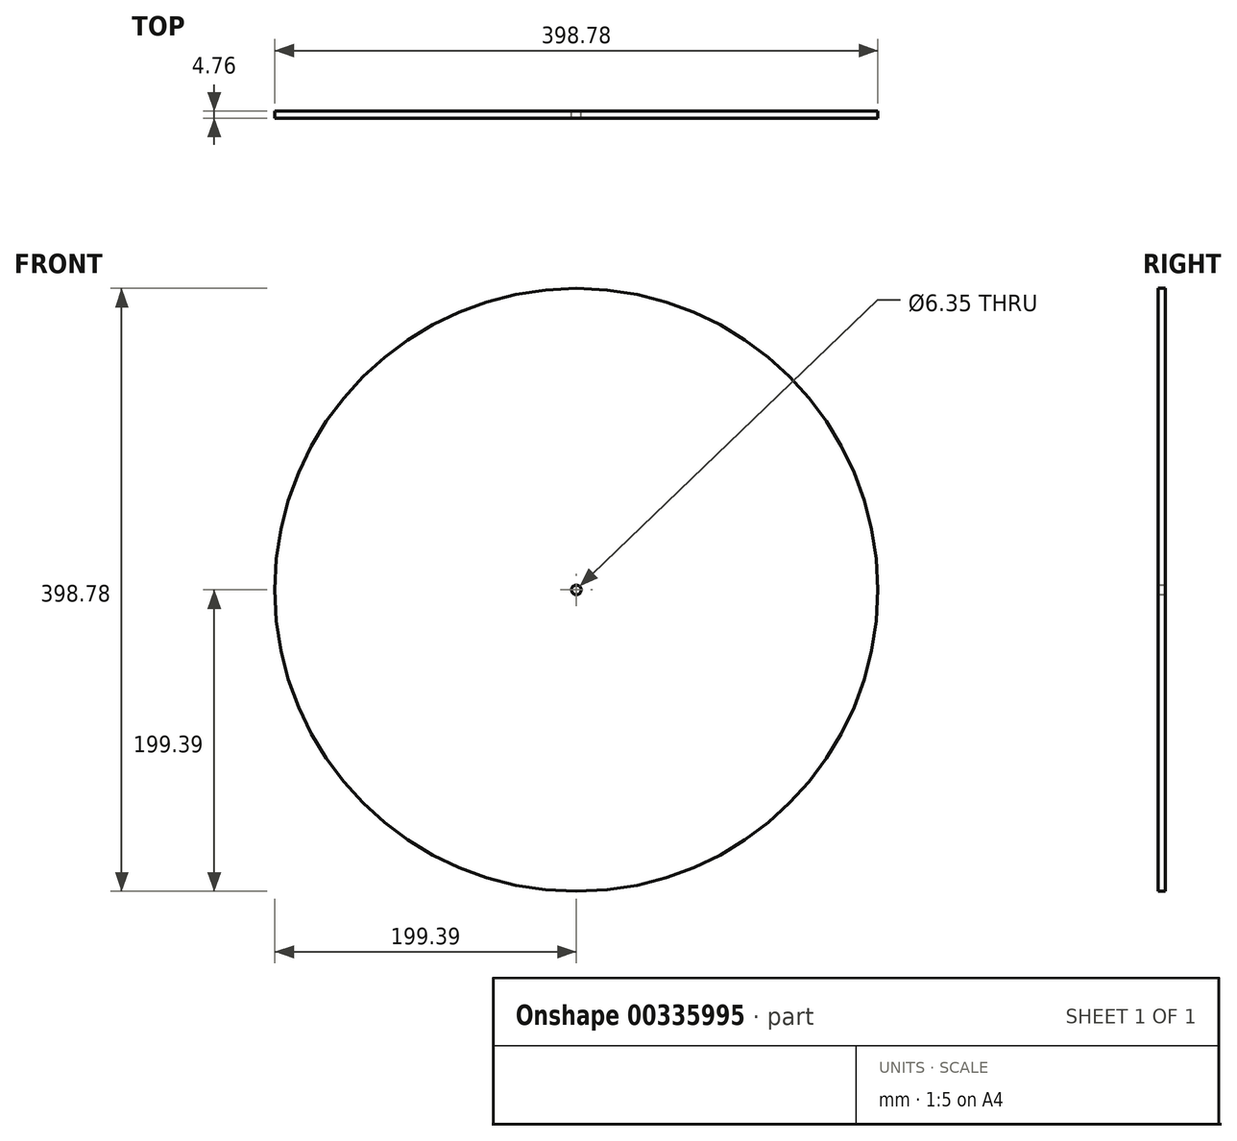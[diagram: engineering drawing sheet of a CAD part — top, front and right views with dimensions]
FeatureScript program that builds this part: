
annotation { "Feature Type Name" : "Feature", "Feature Type Description" : "" }
export const myFeature = defineFeature(function(context is Context, id is Id, definition is map)
    precondition{}
    {
        {
            var Q0;
            Q0=qCreatedBy(makeId("Front.planeOp"),FACE);
            var sketch = newSketch(context, id + "F0", { "sketchPlane" : qUnion([Q0])});
            skCircle(sketch, "E0", {"center": v(0, 0) * mm, "radius": 199.39 * mm});
            skCircle(sketch, "E1", {"center": v(0, 0) * mm, "radius": 3.18 * mm});
            skSolve(sketch);
        }
        {
            var Q0;
            Q0=makeQuery(id+"F0.imprint","IMPRINT",FACE,{"disambiguationData":[TD([[makeQuery(id+"F0.imprint","IMPRINT",EDGE,{"derivedFrom":sQuery(id+"F0.wireOp",EDGE,"E0")}),1.0]])]});
            extrude(context, id + "F1", {"entities" : qUnion([Q0]), "endBound" : BoundingType.SYMMETRIC, "depth" : 4.76 * mm});
        }
    });
